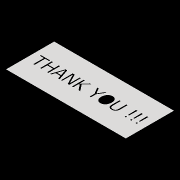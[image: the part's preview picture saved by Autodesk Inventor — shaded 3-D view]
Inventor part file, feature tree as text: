
AUTODESK INVENTOR PART (.ipt)
format: ipt  version: 2018 (Build 220112000, 112)  size: 143,360 bytes
history: native  units: mm
features: plane x1, sketch x1, other x1, surface_op x1
ambient origin geometry x8: Origin, YZ Plane, XZ Plane, XY Plane, X Axis, Y Axis, Z Axis, Center Point
bodies: Body1 (feature_tree)
feature tree (4):
  plane  "Work Plane1"
  sketch  "Sketch2"  dims[d6=10.0mm d7=25.0mm d8=10.0mm]
  other  "Srf1"
  surface_op  "Boundary Patch1"
